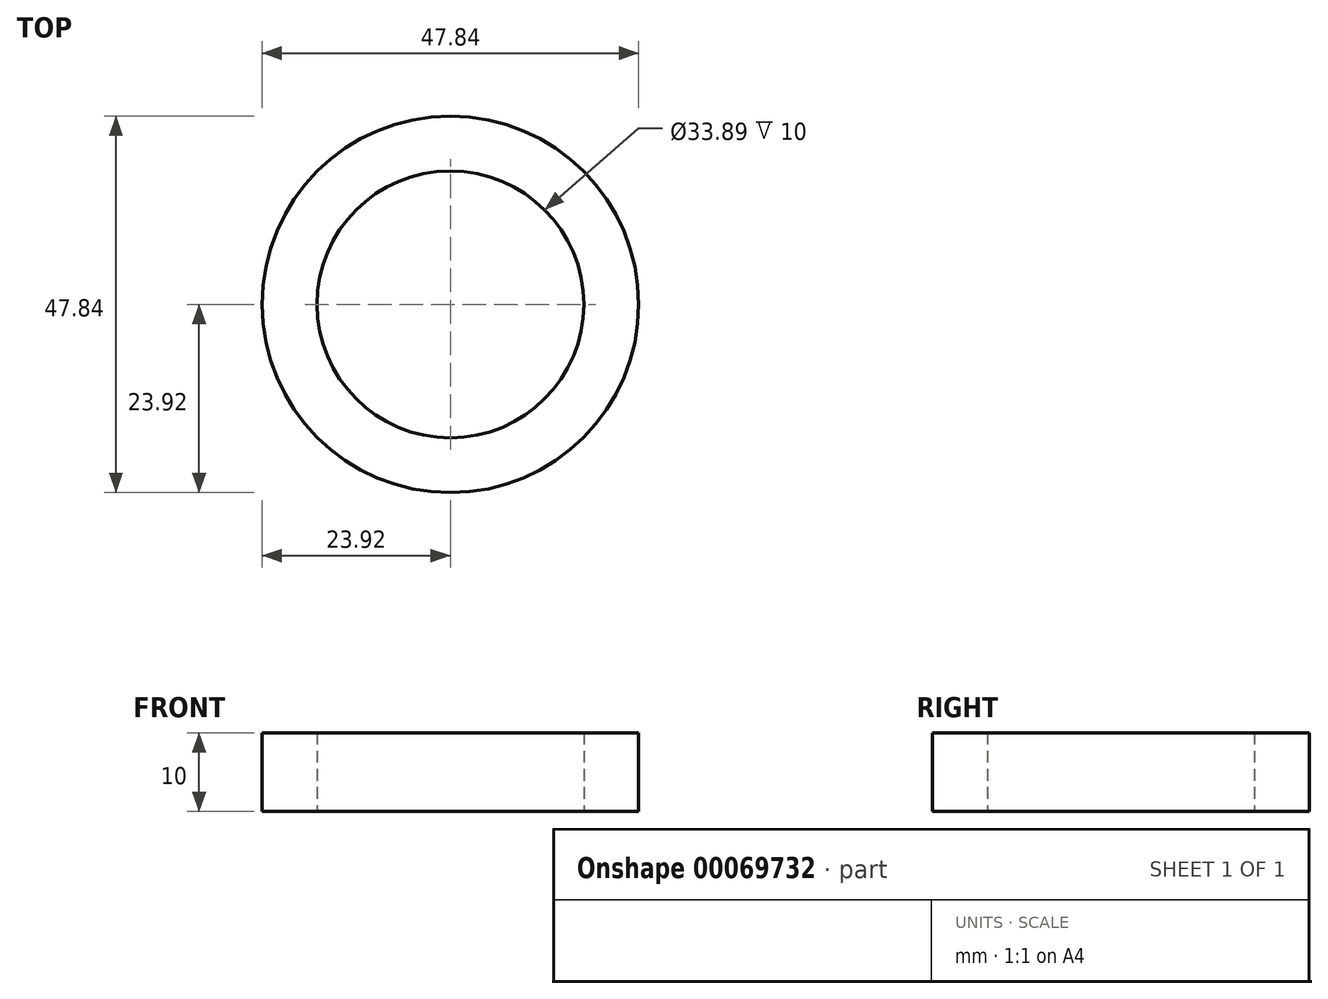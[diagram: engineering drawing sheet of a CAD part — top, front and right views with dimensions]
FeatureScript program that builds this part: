
annotation { "Feature Type Name" : "Feature", "Feature Type Description" : "" }
export const myFeature = defineFeature(function(context is Context, id is Id, definition is map)
    precondition{}
    {
        {
            var Q0;
            Q0=qCreatedBy(makeId("Top.planeOp"),FACE);
            var sketch = newSketch(context, id + "F0", { "sketchPlane" : qUnion([Q0])});
            skCircle(sketch, "E0", {"center": v(0, 0) * mm, "radius": 23.92 * mm});
            skCircle(sketch, "E1", {"center": v(0, 0) * mm, "radius": 16.95 * mm});
            skSolve(sketch);
        }
        {
            var Q0;
            Q0=makeQuery(id+"F0.imprint","IMPRINT",FACE,{"disambiguationData":[TD([[makeQuery(id+"F0.imprint","IMPRINT",EDGE,{"derivedFrom":sQuery(id+"F0.wireOp",EDGE,"E0")}),1.0]])]});
            extrude(context, id + "F1", {"entities" : qUnion([Q0]), "depth" : 10 * mm});
        }
    });
